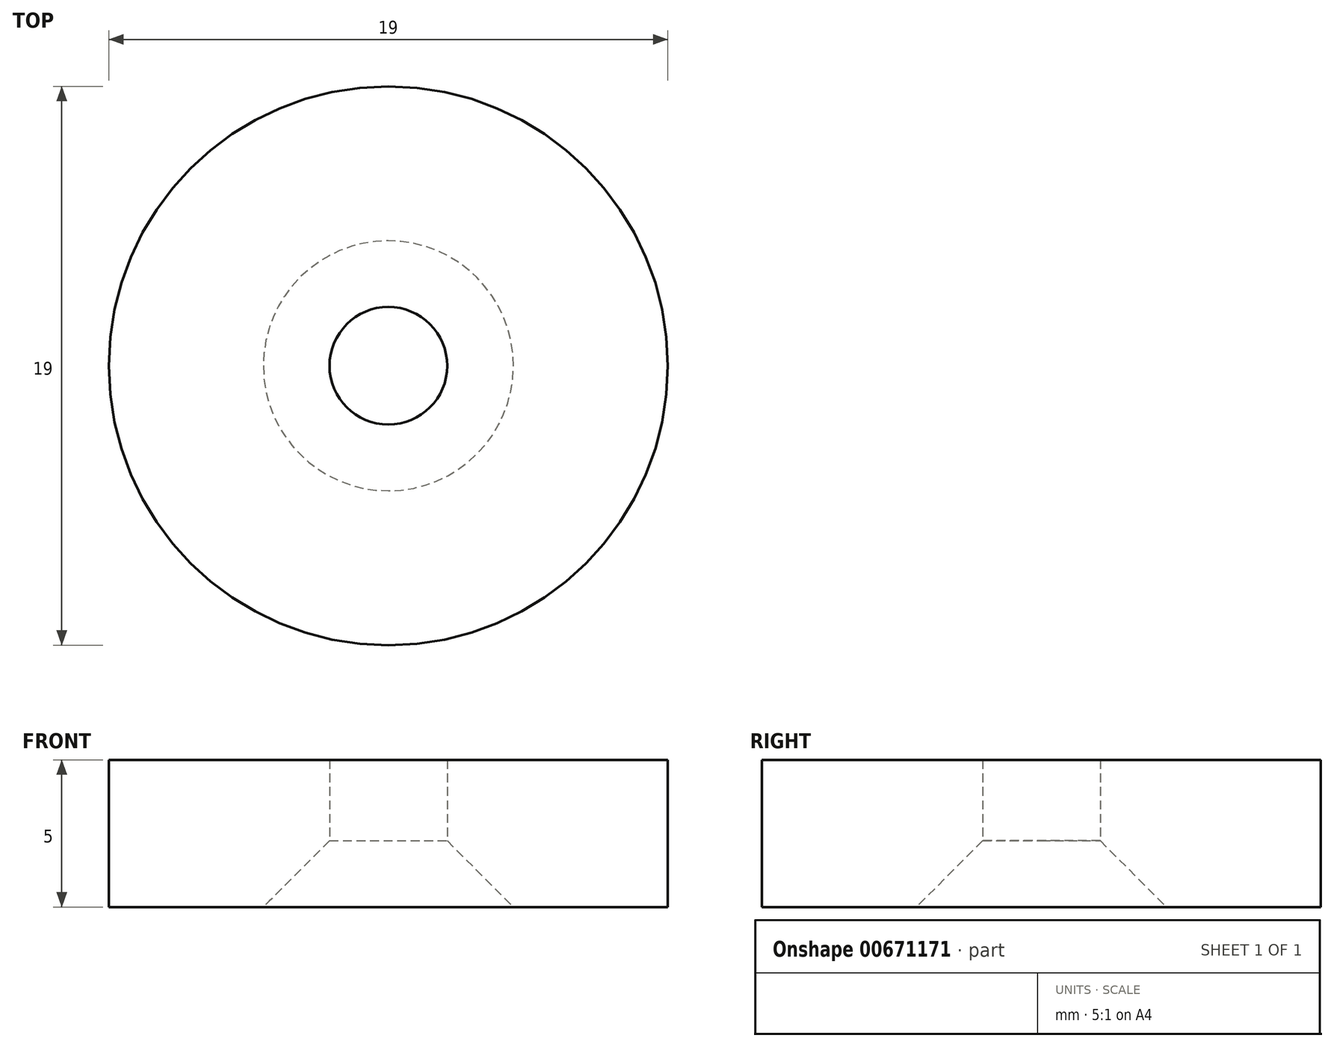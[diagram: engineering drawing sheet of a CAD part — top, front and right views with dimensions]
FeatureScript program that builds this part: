
annotation { "Feature Type Name" : "Feature", "Feature Type Description" : "" }
export const myFeature = defineFeature(function(context is Context, id is Id, definition is map)
    precondition{}
    {
        {
            var Q0;
            Q0=qCreatedBy(makeId("Top.planeOp"),FACE);
            var sketch = newSketch(context, id + "F0", { "sketchPlane" : qUnion([Q0])});
            skCircle(sketch, "E0", {"center": v(0, 0) * mm, "radius": 9.5 * mm});
            skSolve(sketch);
        }
        {
            var Q0;
            Q0 = qSketchRegion(id + "F0", true);
            extrude(context, id + "F1", {"entities" : qUnion([Q0]), "depth" : 5 * mm, "offsetDistance" : 25 * mm});
        }
        {
            var Q0;
            Q0=makeQuery(id+"F1.opExtrude","CAP_FACE",FACE,{"disambiguationData":[OSD([sQuery(id+"F0.wireOp",EDGE,"E0")])],"isStart":true});
            var sketch = newSketch(context, id + "F2", { "sketchPlane" : qUnion([Q0])});
            skPoint(sketch, "E1", {"position": v(0, 0) * mm});
            skSolve(sketch);
        }
        {
            var Q0;
            Q0=sQuery(id+"F2.wireOp",VERTEX,"E1");
            var Q1;
            Q1=makeQuery(id+"F1.opExtrude","SWEPT_BODY",BODY,{"disambiguationData":[OSD([sQuery(id+"F0.wireOp",EDGE,"E0")])]});
            hole(context, id + "F3", {"style" : HoleStyle.C_SINK, "endStyle" : HoleEndStyle.BLIND, "holeDiameter" : 4 * mm, "cSinkDiameter" : 8.5 * mm, "cSinkAngle" : 90 * degree, "majorDiameter" : 5 * mm, "holeDepth" : 5 * mm, "isTappedThrough" : true, "tappedDepth" : 12 * mm, "tapClearance" : 3, "startFromSketch" : true, "locations" : qUnion([Q0]), "scope" : qUnion([Q1])});
        }
    });
